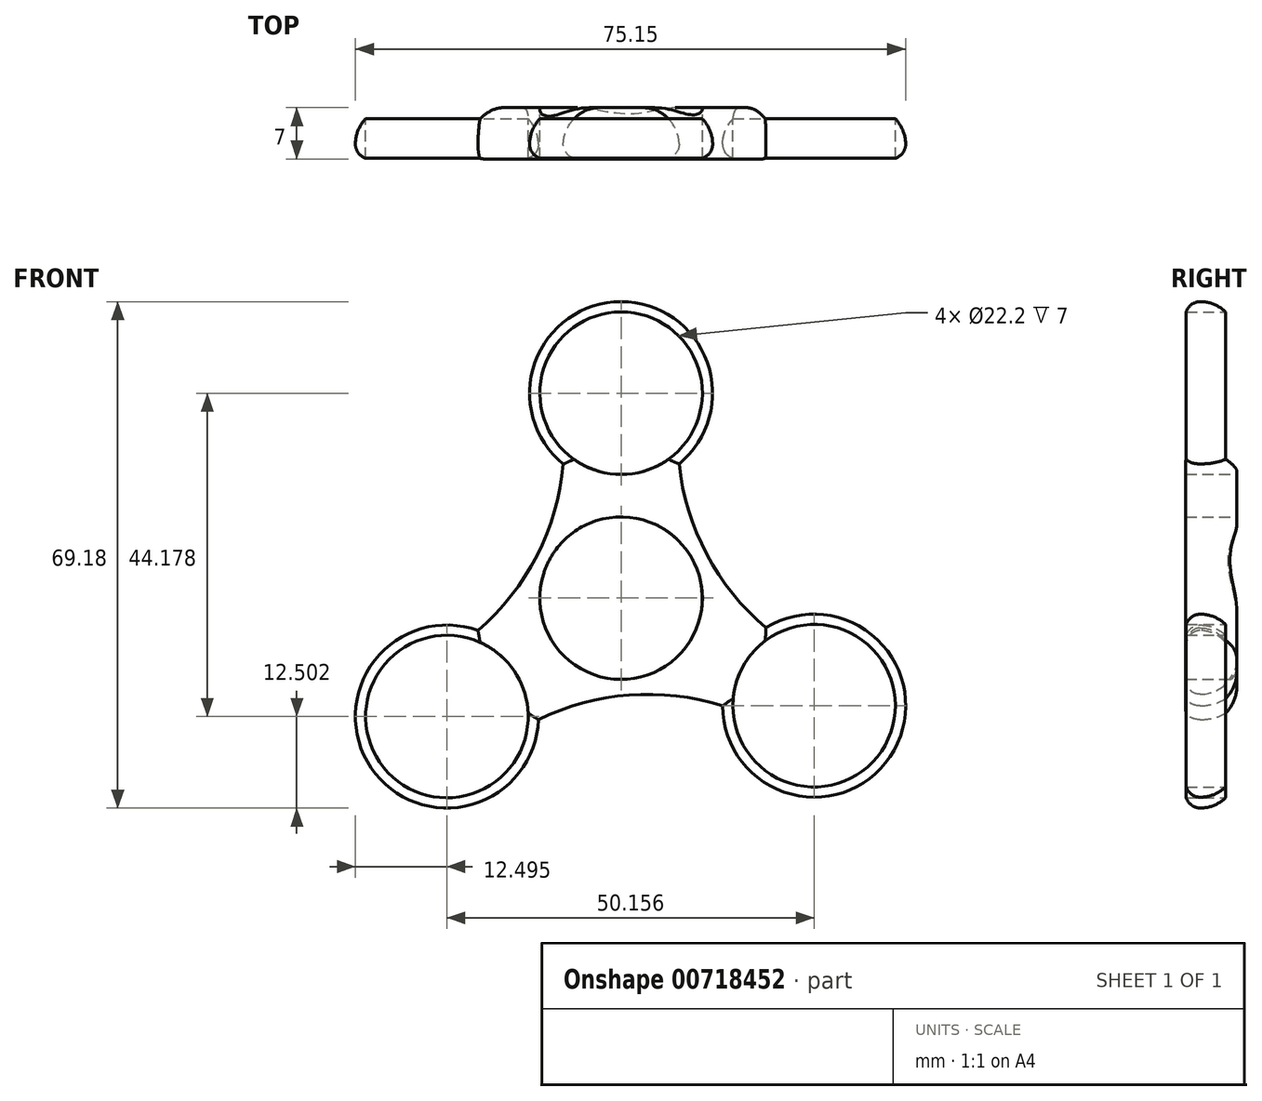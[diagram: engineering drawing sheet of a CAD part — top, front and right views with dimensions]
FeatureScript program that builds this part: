
annotation { "Feature Type Name" : "Feature", "Feature Type Description" : "" }
export const myFeature = defineFeature(function(context is Context, id is Id, definition is map)
    precondition{}
    {
        {
            var Q0;
            Q0=qCreatedBy(makeId("Front.planeOp"),FACE);
            var sketch = newSketch(context, id + "F0", { "sketchPlane" : qUnion([Q0])});
            skCircle(sketch, "E0", {"center": v(0, 28) * mm, "radius": 11.1 * mm});
            skCircle(sketch, "E1.1.0", {"center": v(-23.8, -16.18) * mm, "radius": 11.1 * mm});
            skCircle(sketch, "E1.2.0", {"center": v(26.36, -14.7) * mm, "radius": 11.1 * mm});
            skPoint(sketch, "E1.center", {"position": v(0.86, -0.96) * mm});
            skArc(sketch, "E2", {"start": v(-19.55, -4.42) * mm, "mid": v(-11.5, 5.8) * mm, "end": v(-7.9, 18.3) * mm});
            skArc(sketch, "E3", {"start": v(7.92, 18.33) * mm, "mid": v(11.7, 5.99) * mm, "end": v(19.8, -4.06) * mm});
            skArc(sketch, "E4", {"start": v(13.86, -14.71) * mm, "mid": v(1.1, -13.24) * mm, "end": v(-11.3, -16.6) * mm});
            skCircle(sketch, "E5", {"center": v(0, 0) * mm, "radius": 11.1 * mm});
            skArc(sketch, "E6", {"start": v(7.92, 18.33) * mm, "mid": v(-0.02, 40.5) * mm, "end": v(-7.9, 18.3) * mm});
            skArc(sketch, "E7", {"start": v(13.86, -14.71) * mm, "mid": v(37.28, -20.78) * mm, "end": v(19.8, -4.06) * mm});
            skArc(sketch, "E8", {"start": v(-19.55, -4.42) * mm, "mid": v(-34.15, -23.18) * mm, "end": v(-11.3, -16.6) * mm});
            skPoint(sketch, "E9.orphan", {"position": v(-7.78, 20.09) * mm});
            skPoint(sketch, "E10.orphan", {"position": v(7.78, 20.09) * mm});
            skSolve(sketch);
        }
        {
            var Q0;
            Q0 = qSketchRegion(id + "F0", true);
            extrude(context, id + "F1", {"entities" : qUnion([Q0]), "depth" : 7 * mm, "offsetDistance" : 25 * mm});
        }
        {
            var Q0;
            Q0=makeQuery(id+"F1.opExtrude","CAP_EDGE",EDGE,{"disambiguationData":[OSD([sQuery(id+"F0.wireOp",EDGE,"E6")])],"isStart":false});
            var Q1;
            Q1=makeQuery(id+"F1.opExtrude","CAP_EDGE",EDGE,{"disambiguationData":[OSD([sQuery(id+"F0.wireOp",EDGE,"E3")])],"isStart":false});
            var Q2;
            Q2=makeQuery(id+"F1.opExtrude","CAP_EDGE",EDGE,{"disambiguationData":[OSD([sQuery(id+"F0.wireOp",EDGE,"E7")])],"isStart":false});
            var Q3;
            Q3=makeQuery(id+"F1.opExtrude","CAP_EDGE",EDGE,{"disambiguationData":[OSD([sQuery(id+"F0.wireOp",EDGE,"E4")])],"isStart":false});
            var Q4;
            Q4=makeQuery(id+"F1.opExtrude","CAP_EDGE",EDGE,{"disambiguationData":[OSD([sQuery(id+"F0.wireOp",EDGE,"E8")])],"isStart":false});
            var Q5;
            Q5=makeQuery(id+"F1.opExtrude","CAP_EDGE",EDGE,{"disambiguationData":[OSD([sQuery(id+"F0.wireOp",EDGE,"E2")])],"isStart":false});
            fillet(context, id + "F2", {"entities" : qUnion([Q0, Q1, Q2, Q3, Q4, Q5]), "radius" : 2 * mm, "tangentPropagation" : true, "allowEdgeOverflow" : false});
        }
        {
            var Q0;
            Q0=makeQuery(id+"F1.opExtrude","CAP_EDGE",EDGE,{"disambiguationData":[OSD([sQuery(id+"F0.wireOp",EDGE,"E8")])],"isStart":true});
            var Q1;
            Q1=makeQuery(id+"F1.opExtrude","CAP_EDGE",EDGE,{"disambiguationData":[OSD([sQuery(id+"F0.wireOp",EDGE,"E4")])],"isStart":true});
            var Q2;
            Q2=makeQuery(id+"F1.opExtrude","CAP_EDGE",EDGE,{"disambiguationData":[OSD([sQuery(id+"F0.wireOp",EDGE,"E7")])],"isStart":true});
            var Q3;
            Q3=makeQuery(id+"F1.opExtrude","CAP_EDGE",EDGE,{"disambiguationData":[OSD([sQuery(id+"F0.wireOp",EDGE,"E3")])],"isStart":true});
            var Q4;
            Q4=makeQuery(id+"F1.opExtrude","CAP_EDGE",EDGE,{"disambiguationData":[OSD([sQuery(id+"F0.wireOp",EDGE,"E6")])],"isStart":true});
            var Q5;
            Q5=makeQuery(id+"F1.opExtrude","CAP_EDGE",EDGE,{"disambiguationData":[OSD([sQuery(id+"F0.wireOp",EDGE,"E2")])],"isStart":true});
            fillet(context, id + "F3", {"entities" : qUnion([Q0, Q1, Q2, Q3, Q4, Q5]), "radius" : 5 * mm, "tangentPropagation" : true, "allowEdgeOverflow" : false});
        }
    });
